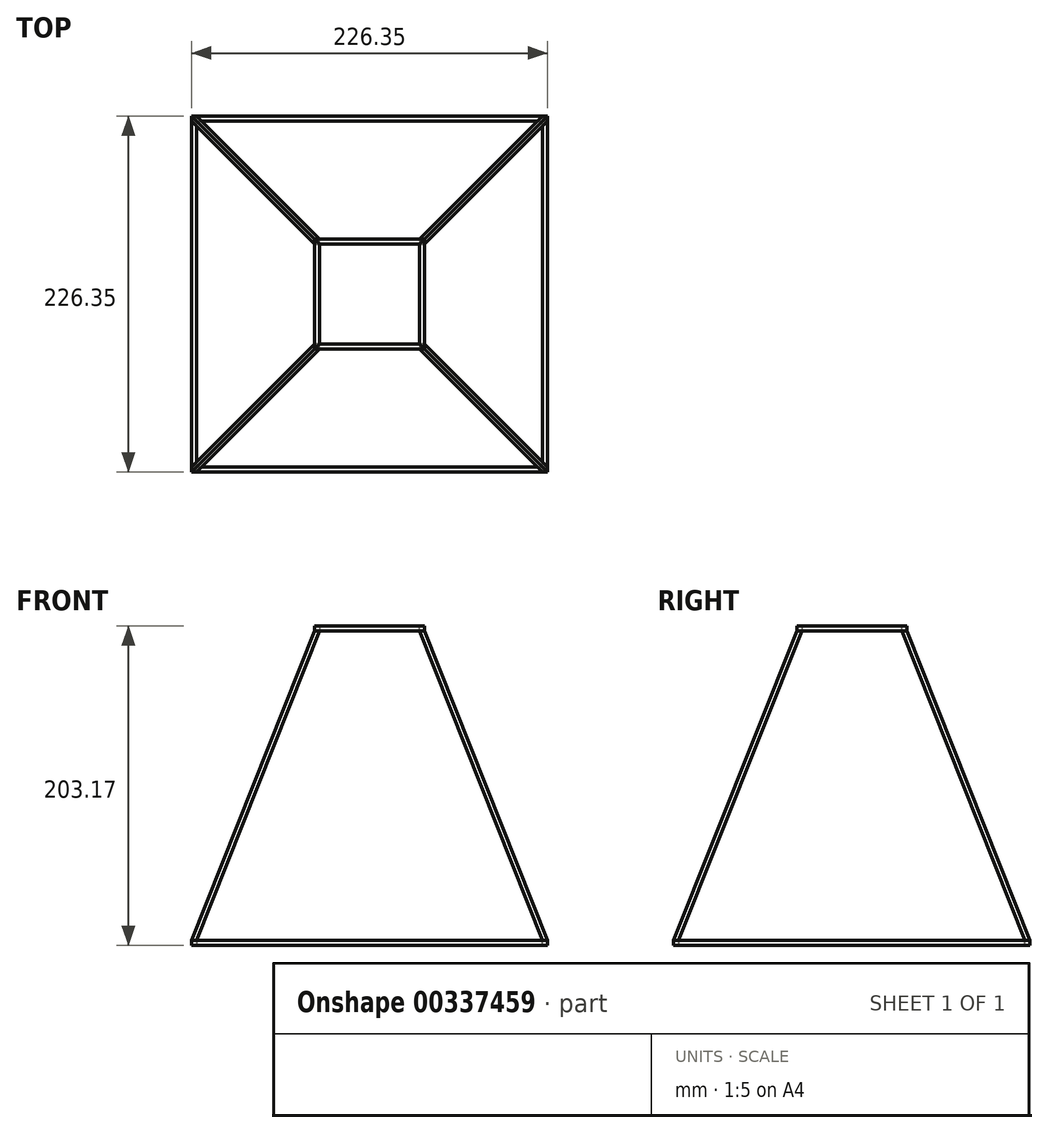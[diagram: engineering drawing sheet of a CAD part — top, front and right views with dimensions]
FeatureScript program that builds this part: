
annotation { "Feature Type Name" : "Feature", "Feature Type Description" : "" }
export const myFeature = defineFeature(function(context is Context, id is Id, definition is map)
    precondition{}
    {
        {
            var Q0;
            Q0=qCreatedBy(makeId("Front.planeOp"),FACE);
            var sketch = newSketch(context, id + "F0", { "sketchPlane" : qUnion([Q0])});
            skLineSegment(sketch, "E0.bottom", {"start": v(0, 3.17) * mm, "end": v(3.18, 3.17) * mm});
            skLineSegment(sketch, "E0.top", {"start": v(0, 0) * mm, "end": v(3.18, 0) * mm});
            skLineSegment(sketch, "E0.left", {"start": v(0, 3.17) * mm, "end": v(0, 0) * mm});
            skLineSegment(sketch, "E0.right", {"start": v(3.18, 3.17) * mm, "end": v(3.18, 0) * mm});
            skLineSegment(sketch, "E1.bottom", {"start": v(223.18, 3.18) * mm, "end": v(226.35, 3.18) * mm});
            skLineSegment(sketch, "E1.top", {"start": v(223.18, 0) * mm, "end": v(226.35, 0) * mm});
            skLineSegment(sketch, "E1.left", {"start": v(226.35, 3.18) * mm, "end": v(226.35, 0) * mm});
            skLineSegment(sketch, "E1.right", {"start": v(223.18, 3.18) * mm, "end": v(223.18, 0) * mm});
            skSolve(sketch);
        }
        {
            var Q0;
            Q0 = qSketchRegion(id + "F0", true);
            extrude(context, id + "F1", {"entities" : qUnion([Q0]), "depth" : 226.35 * mm});
        }
        {
            var Q0;
            Q0=makeQuery(id+"F1.opExtrude","CAP_EDGE",EDGE,{"disambiguationData":[OSD([sQuery(id+"F0.wireOp",EDGE,"E0.right")])],"isStart":false});
            var Q1;
            Q1=makeQuery(id+"F1.opExtrude","CAP_EDGE",EDGE,{"disambiguationData":[OSD([sQuery(id+"F0.wireOp",EDGE,"E1.right")])],"isStart":false});
            var Q2;
            Q2=makeQuery(id+"F1.opExtrude","CAP_EDGE",EDGE,{"disambiguationData":[OSD([sQuery(id+"F0.wireOp",EDGE,"E1.right")])],"isStart":true});
            var Q3;
            Q3=makeQuery(id+"F1.opExtrude","CAP_EDGE",EDGE,{"disambiguationData":[OSD([sQuery(id+"F0.wireOp",EDGE,"E0.right")])],"isStart":true});
            chamfer(context, id + "F2", {"entities" : qUnion([Q0, Q1, Q2, Q3]), "width" : 3.17 * mm, "tangentPropagation" : true});
        }
        {
            var Q0;
            Q0=qCreatedBy(makeId("Front.planeOp"),FACE);
            cPlane(context, id + "F3", {"entities" : qUnion([Q0]), "cplaneType" : CPlaneType.OFFSET, "offset" : 113.18 * mm, "width" : 150 * mm, "height" : 150 * mm});
        }
        {
            var Q0;
            Q0=qCreatedBy(id+"F3.planeOp",FACE);
            var sketch = newSketch(context, id + "F4", { "sketchPlane" : qUnion([Q0])});
            skLineSegment(sketch, "E2", {"start": v(113.17, 10) * mm, "end": v(113.17, 0) * mm});
            skLineSegment(sketch, "E3", {"start": v(3.18, 0) * mm, "end": v(223.18, 0) * mm});
            skSolve(sketch);
        }
        {
            var Q0;
            Q0=makeQuery(id+"F1.opExtrude","SWEPT_BODY",BODY,{"disambiguationData":[OSD([sQuery(id+"F0.wireOp",EDGE,"E0.bottom"),sQuery(id+"F0.wireOp",EDGE,"E0.top"),sQuery(id+"F0.wireOp",EDGE,"E0.left"),sQuery(id+"F0.wireOp",EDGE,"E0.right")])]});
            var Q1;
            Q1=makeQuery(id+"F1.opExtrude","SWEPT_BODY",BODY,{"disambiguationData":[OSD([sQuery(id+"F0.wireOp",EDGE,"E1.bottom"),sQuery(id+"F0.wireOp",EDGE,"E1.top"),sQuery(id+"F0.wireOp",EDGE,"E1.left"),sQuery(id+"F0.wireOp",EDGE,"E1.right")])]});
            var Q2;
            Q2=sQuery(id+"F4.wireOp",EDGE,"E2");
            transform(context, id + "F5", {"entities" : qUnion([Q0, Q1]), "transformType" : TransformType.ROTATION, "transformAxis" : qUnion([Q2]), "angle" : 90 * degree, "makeCopy" : true});
        }
        {
            var Q0;
            Q0=qCreatedBy(makeId("Top.planeOp"),FACE);
            cPlane(context, id + "F6", {"entities" : qUnion([Q0]), "cplaneType" : CPlaneType.OFFSET, "offset" : 200 * mm, "width" : 150 * mm, "height" : 150 * mm});
        }
        {
            var Q0;
            Q0=qCreatedBy(id+"F6.planeOp",FACE);
            var sketch = newSketch(context, id + "F7", { "sketchPlane" : qUnion([Q0])});
            skLineSegment(sketch, "E4.bottom", {"start": v(145, -78.17) * mm, "end": v(148.17, -78.17) * mm});
            skLineSegment(sketch, "E4.top", {"start": v(145, -148.18) * mm, "end": v(148.17, -148.18) * mm});
            skLineSegment(sketch, "E4.left", {"start": v(145, -148.18) * mm, "end": v(145, -78.17) * mm});
            skLineSegment(sketch, "E4.right", {"start": v(148.18, -148.18) * mm, "end": v(148.18, -78.17) * mm});
            skLineSegment(sketch, "E5.bottom", {"start": v(78.17, -78.18) * mm, "end": v(81.35, -78.18) * mm});
            skLineSegment(sketch, "E5.top", {"start": v(78.17, -148.18) * mm, "end": v(81.35, -148.18) * mm});
            skLineSegment(sketch, "E5.left", {"start": v(78.18, -148.18) * mm, "end": v(78.18, -78.18) * mm});
            skLineSegment(sketch, "E5.right", {"start": v(81.35, -148.18) * mm, "end": v(81.35, -78.18) * mm});
            skLineSegment(sketch, "E6", {"start": v(78.18, -113.18) * mm, "end": v(3.18, -113.18) * mm});
            skLineSegment(sketch, "E7", {"start": v(148.18, -113.18) * mm, "end": v(223.18, -113.18) * mm});
            skLineSegment(sketch, "E8", {"start": v(145, -113.18) * mm, "end": v(81.35, -113.18) * mm});
            skLineSegment(sketch, "E9", {"start": v(113.17, -113.18) * mm, "end": v(113.17, -223.18) * mm});
            skLineSegment(sketch, "E10", {"start": v(113.17, -113.18) * mm, "end": v(113.17, -3.18) * mm});
            skSolve(sketch);
        }
        {
            var Q0;
            Q0 = qSketchRegion(id + "F7", true);
            extrude(context, id + "F8", {"entities" : qUnion([Q0]), "depth" : 3.17 * mm});
        }
        {
            var Q0;
            Q0=makeQuery(id+"F8.opExtrude","SWEPT_EDGE",EDGE,{"disambiguationData":[OSD([sQuery(id+"F7.wireOp",EDGE,"E5.top"),sQuery(id+"F7.wireOp",EDGE,"E5.right")])]});
            var Q1;
            Q1=makeQuery(id+"F8.opExtrude","SWEPT_EDGE",EDGE,{"disambiguationData":[OSD([sQuery(id+"F7.wireOp",EDGE,"E4.top"),sQuery(id+"F7.wireOp",EDGE,"E4.left")])]});
            var Q2;
            Q2=makeQuery(id+"F8.opExtrude","SWEPT_EDGE",EDGE,{"disambiguationData":[OSD([sQuery(id+"F7.wireOp",EDGE,"E5.bottom"),sQuery(id+"F7.wireOp",EDGE,"E5.right")])]});
            var Q3;
            Q3=makeQuery(id+"F8.opExtrude","SWEPT_EDGE",EDGE,{"disambiguationData":[OSD([sQuery(id+"F7.wireOp",EDGE,"E4.bottom"),sQuery(id+"F7.wireOp",EDGE,"E4.left")])]});
            chamfer(context, id + "F9", {"entities" : qUnion([Q0, Q1, Q2, Q3]), "width" : 3.17 * mm, "tangentPropagation" : true});
        }
        {
            var Q0;
            Q0=makeQuery(id+"F8.opExtrude","SWEPT_BODY",BODY,{"disambiguationData":[OSD([sQuery(id+"F7.wireOp",EDGE,"E5.bottom"),sQuery(id+"F7.wireOp",EDGE,"E5.top"),sQuery(id+"F7.wireOp",EDGE,"E5.left"),sQuery(id+"F7.wireOp",EDGE,"E5.right")])]});
            var Q1;
            Q1=makeQuery(id+"F8.opExtrude","SWEPT_BODY",BODY,{"disambiguationData":[OSD([sQuery(id+"F7.wireOp",EDGE,"E4.bottom"),sQuery(id+"F7.wireOp",EDGE,"E4.top"),sQuery(id+"F7.wireOp",EDGE,"E4.left"),sQuery(id+"F7.wireOp",EDGE,"E4.right")])]});
            var Q2;
            Q2=sQuery(id+"F4.wireOp",EDGE,"E2");
            transform(context, id + "F10", {"entities" : qUnion([Q0, Q1]), "transformType" : TransformType.ROTATION, "transformAxis" : qUnion([Q2]), "angle" : 90 * degree, "makeCopy" : true});
        }
        {
            var Q0;
            {var subQ0=sQuery(id+"F7.wireOp",EDGE,"E4.left");var subQ1=sQuery(id+"F7.wireOp",EDGE,"E4.top");Q0=makeQuery(id+"F9.opChamfer","BLEND_VERTEX",VERTEX,{"blendedFrom":[makeQuery(id+"F8.opExtrude","SWEPT_EDGE",EDGE,{"disambiguationData":[OSD([subQ1,subQ0])]}),makeQuery(id+"F8.opExtrude","CAP_FACE",FACE,{"disambiguationData":[OSD([sQuery(id+"F7.wireOp",EDGE,"E4.bottom"),subQ1,subQ0,sQuery(id+"F7.wireOp",EDGE,"E4.right")])],"isStart":false}),makeQuery(id+"F8.opExtrude","SWEPT_FACE",FACE,{"disambiguationData":[OSD([subQ0])]})],"blendedInto":[makeQuery(id+"F8.opExtrude","CAP_FACE",FACE,{"disambiguationData":[OSD([sQuery(id+"F7.wireOp",EDGE,"E4.bottom"),subQ1,subQ0,sQuery(id+"F7.wireOp",EDGE,"E4.right")])],"isStart":false}),makeQuery(id+"F8.opExtrude","SWEPT_FACE",FACE,{"disambiguationData":[OSD([subQ0])]})]});}
            var Q1;
            {var subQ0=sQuery(id+"F7.wireOp",EDGE,"E4.right");var subQ1=sQuery(id+"F7.wireOp",EDGE,"E4.left");var subQ2=sQuery(id+"F7.wireOp",EDGE,"E4.top");Q1=makeQuery(id+"F9.opChamfer","BLEND_VERTEX",VERTEX,{"blendedFrom":[makeQuery(id+"F8.opExtrude","SWEPT_EDGE",EDGE,{"disambiguationData":[OSD([subQ2,subQ1])]}),makeQuery(id+"F8.opExtrude","CAP_FACE",FACE,{"disambiguationData":[OSD([sQuery(id+"F7.wireOp",EDGE,"E4.bottom"),subQ2,subQ1,subQ0])],"isStart":false}),makeQuery(id+"F8.opExtrude","SWEPT_FACE",FACE,{"disambiguationData":[OSD([subQ0])]})],"blendedInto":[makeQuery(id+"F8.opExtrude","CAP_FACE",FACE,{"disambiguationData":[OSD([sQuery(id+"F7.wireOp",EDGE,"E4.bottom"),subQ2,subQ1,subQ0])],"isStart":false}),makeQuery(id+"F8.opExtrude","SWEPT_FACE",FACE,{"disambiguationData":[OSD([subQ0])]})]});}
            var Q2;
            Q2=makeQuery(id+"F2.opChamfer","BLEND_VERTEX",VERTEX,{"blendedFrom":[makeQuery(id+"F1.opExtrude","CAP_EDGE",EDGE,{"disambiguationData":[OSD([sQuery(id+"F0.wireOp",EDGE,"E1.right")])],"isStart":false}),makeQuery(id+"F1.opExtrude","SWEPT_FACE",FACE,{"disambiguationData":[OSD([sQuery(id+"F0.wireOp",EDGE,"E1.bottom")])]}),makeQuery(id+"F1.opExtrude","SWEPT_FACE",FACE,{"disambiguationData":[OSD([sQuery(id+"F0.wireOp",EDGE,"E1.left")])]})],"blendedInto":[makeQuery(id+"F1.opExtrude","SWEPT_FACE",FACE,{"disambiguationData":[OSD([sQuery(id+"F0.wireOp",EDGE,"E1.bottom")])]}),makeQuery(id+"F1.opExtrude","SWEPT_FACE",FACE,{"disambiguationData":[OSD([sQuery(id+"F0.wireOp",EDGE,"E1.left")])]})]});
            cPlane(context, id + "F11", {"entities" : qUnion([Q0, Q1, Q2]), "cplaneType" : CPlaneType.THREE_POINT, "offset" : 25 * mm, "width" : 150 * mm, "height" : 150 * mm});
        }
        {
            var Q0;
            Q0=qCreatedBy(id+"F6.planeOp",FACE);
            var sketch = newSketch(context, id + "F12", { "sketchPlane" : qUnion([Q0])});
            skLineSegment(sketch, "E11.bottom", {"start": v(78.18, -81.35) * mm, "end": v(81.35, -81.35) * mm});
            skLineSegment(sketch, "E11.top", {"start": v(78.18, -78.18) * mm, "end": v(81.35, -78.18) * mm});
            skLineSegment(sketch, "E11.left", {"start": v(78.18, -81.35) * mm, "end": v(78.18, -78.18) * mm});
            skLineSegment(sketch, "E11.right", {"start": v(81.35, -81.35) * mm, "end": v(81.35, -78.18) * mm});
            skSolve(sketch);
        }
        {
            var Q0;
            Q0=makeQuery(id+"F2.opChamfer","BLEND_EDGE",EDGE,{"blendedFrom":[makeQuery(id+"F1.opExtrude","CAP_EDGE",EDGE,{"disambiguationData":[OSD([sQuery(id+"F0.wireOp",EDGE,"E0.right")])],"isStart":true}),makeQuery(id+"F1.opExtrude","SWEPT_FACE",FACE,{"disambiguationData":[OSD([sQuery(id+"F0.wireOp",EDGE,"E0.bottom")])]})],"blendedInto":[makeQuery(id+"F1.opExtrude","SWEPT_FACE",FACE,{"disambiguationData":[OSD([sQuery(id+"F0.wireOp",EDGE,"E0.bottom")])]})]});
            cPoint(context, id + "F13", {"entities" : qUnion([Q0]), "parameter" : 0.5});
        }
        {
            var Q0;
            Q0=makeQuery(id+"F2.opChamfer","BLEND_EDGE",EDGE,{"blendedFrom":[makeQuery(id+"F1.opExtrude","CAP_EDGE",EDGE,{"disambiguationData":[OSD([sQuery(id+"F0.wireOp",EDGE,"E1.right")])],"isStart":true}),makeQuery(id+"F1.opExtrude","SWEPT_FACE",FACE,{"disambiguationData":[OSD([sQuery(id+"F0.wireOp",EDGE,"E1.bottom")])]})],"blendedInto":[makeQuery(id+"F1.opExtrude","SWEPT_FACE",FACE,{"disambiguationData":[OSD([sQuery(id+"F0.wireOp",EDGE,"E1.bottom")])]})]});
            cPoint(context, id + "F14", {"entities" : qUnion([Q0]), "parameter" : 0.5});
        }
        {
            var Q0;
            Q0 = qCreatedBy(id + "F13" ,VERTEX);
            var Q1;
            Q1 = qCreatedBy(id + "F14" ,VERTEX);
            var Q2;
            {var subQ0=sQuery(id+"F0.wireOp",EDGE,"E1.right");Q2=makeQuery(id+"F2.opChamfer","BLEND_VERTEX",VERTEX,{"blendedFrom":[makeQuery(id+"F1.opExtrude","CAP_EDGE",EDGE,{"disambiguationData":[OSD([subQ0])],"isStart":false}),makeQuery(id+"F1.opExtrude","SWEPT_FACE",FACE,{"disambiguationData":[OSD([sQuery(id+"F0.wireOp",EDGE,"E1.bottom")])]}),makeQuery(id+"F1.opExtrude","SWEPT_FACE",FACE,{"disambiguationData":[OSD([subQ0])]})],"blendedInto":[makeQuery(id+"F1.opExtrude","SWEPT_FACE",FACE,{"disambiguationData":[OSD([sQuery(id+"F0.wireOp",EDGE,"E1.bottom")])]}),makeQuery(id+"F1.opExtrude","SWEPT_FACE",FACE,{"disambiguationData":[OSD([subQ0])]})]});}
            cPlane(context, id + "F15", {"entities" : qUnion([Q0, Q1, Q2]), "cplaneType" : CPlaneType.THREE_POINT, "offset" : 25 * mm, "width" : 150 * mm, "height" : 150 * mm});
        }
        {
            var Q0;
            Q0=qCreatedBy(id+"F15.planeOp",FACE);
            var sketch = newSketch(context, id + "F16", { "sketchPlane" : qUnion([Q0])});
            skPoint(sketch, "E12", {"position": v(1.59, -1.59) * mm});
            skSolve(sketch);
        }
        {
            var Q0;
            Q0=qCreatedBy(id+"F6.planeOp",FACE);
            var sketch = newSketch(context, id + "F17", { "sketchPlane" : qUnion([Q0])});
            skPoint(sketch, "E13", {"position": v(79.76, -79.76) * mm});
            skSolve(sketch);
        }
        {
            var Q0;
            Q0=qCreatedBy(id+"F11.planeOp",FACE);
            var sketch = newSketch(context, id + "F18", { "sketchPlane" : qUnion([Q0])});
            skLineSegment(sketch, "E14", {"start": v(2.25, 3.17) * mm, "end": v(112.8, 200) * mm});
            skSolve(sketch);
        }
        {
            var Q0;
            Q0 = qSketchRegion(id + "F12", true);
            var Q1;
            Q1 = qConstructionFilter(qBodyType(qCreatedBy(id + "F18" ,EDGE), BodyType.WIRE), ConstructionObject.NO);
            sweep(context, id + "F19", {"profiles" : qUnion([Q0]), "path" : qUnion([Q1])});
        }
        {
            var Q0;
            Q0=makeQuery(id+"F19.opSweep","SWEPT_BODY",BODY,{"disambiguationData":[OSD([sQuery(id+"F12.wireOp",EDGE,"E11.bottom"),sQuery(id+"F12.wireOp",EDGE,"E11.top"),sQuery(id+"F12.wireOp",EDGE,"E11.left"),sQuery(id+"F12.wireOp",EDGE,"E11.right"),sQuery(id+"F18.wireOp",EDGE,"E14")])]});
            var Q1;
            Q1=sQuery(id+"F4.wireOp",EDGE,"E2");
            transform(context, id + "F20", {"entities" : qUnion([Q0]), "transformType" : TransformType.ROTATION, "transformAxis" : qUnion([Q1]), "angle" : 90 * degree, "makeCopy" : true});
        }
        {
            var Q0;
            Q0=makeQuery(id+"F19.opSweep","SWEPT_BODY",BODY,{"disambiguationData":[OSD([sQuery(id+"F12.wireOp",EDGE,"E11.bottom"),sQuery(id+"F12.wireOp",EDGE,"E11.top"),sQuery(id+"F12.wireOp",EDGE,"E11.left"),sQuery(id+"F12.wireOp",EDGE,"E11.right"),sQuery(id+"F18.wireOp",EDGE,"E14")])]});
            var Q1;
            Q1=makeQuery(id+"F20.opPattern","COPY",BODY,{"derivedFrom":makeQuery(id+"F19.opSweep","SWEPT_BODY",BODY,{"disambiguationData":[OSD([sQuery(id+"F12.wireOp",EDGE,"E11.bottom"),sQuery(id+"F12.wireOp",EDGE,"E11.top"),sQuery(id+"F12.wireOp",EDGE,"E11.left"),sQuery(id+"F12.wireOp",EDGE,"E11.right"),sQuery(id+"F18.wireOp",EDGE,"E14")])]}),"instanceName":"1"});
            var Q2;
            Q2=sQuery(id+"F4.wireOp",EDGE,"E2");
            transform(context, id + "F21", {"entities" : qUnion([Q0, Q1]), "transformType" : TransformType.ROTATION, "transformAxis" : qUnion([Q2]), "angle" : 180 * degree, "makeCopy" : true});
        }
    });
